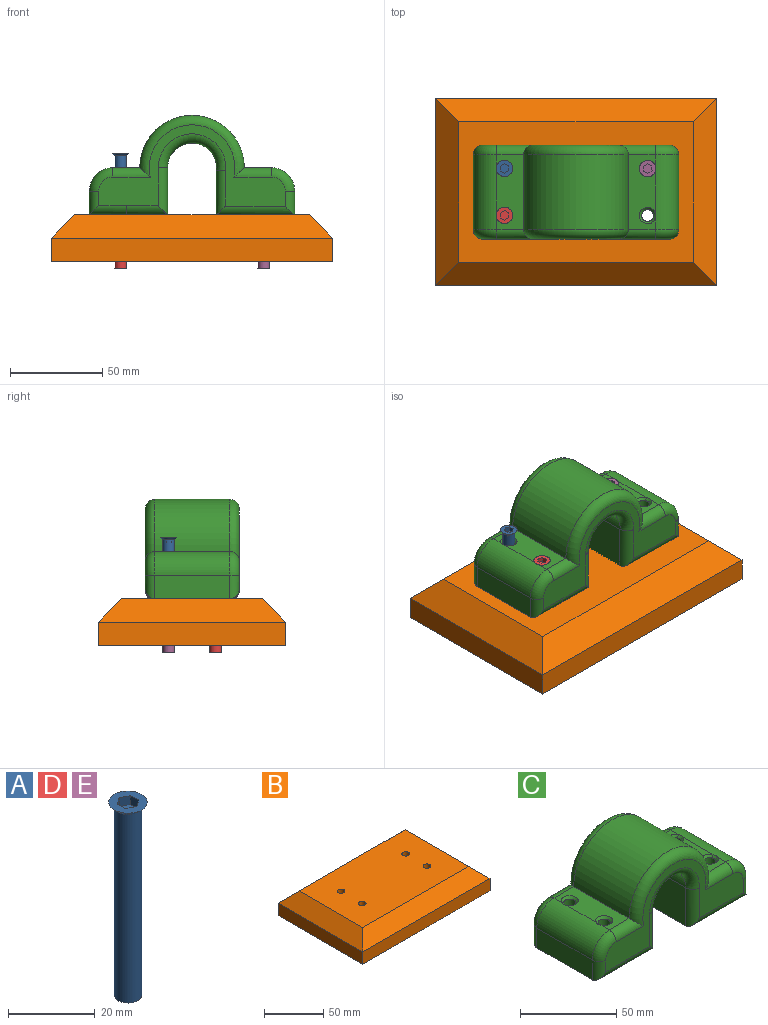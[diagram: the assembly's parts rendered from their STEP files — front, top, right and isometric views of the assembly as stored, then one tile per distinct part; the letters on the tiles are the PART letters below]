
ASSEMBLY  parts=5 mates=4
PART A: 11 faces, bbox 8.9x8.9x54.6 mm
  f0: plane 8.89x8.89mm, normal (0,0,1), area 43.8mm2, adj f3,f4,f5,f6,f7,f8,f9
  f1: cylinder r=3.17mm len=53.34mm, axis (0,0,-1), area 1064.1mm2, adj f2,f3
  f2: plane 6.35x6.35mm, normal (0,0,-1), area 31.7mm2, adj f1
  f3: cone r=4.45mm half-angle=45deg, axis (0,0,1), area 43mm2, adj f0,f1
  f4: plane 2.54x2.38mm, normal (-0.44,-0.9,0), area 6.7mm2, adj f0,f5,f9,f10
  f5: plane 2.54x2.2mm, normal (0.56,-0.83,0), area 6.7mm2, adj f0,f4,f6,f10
  f6: plane 2.64x2.54mm, normal (1,0.07,0), area 6.7mm2, adj f0,f5,f7,f10
  f7: plane 2.54x2.38mm, normal (0.44,0.9,0), area 6.7mm2, adj f0,f6,f8,f10
  f8: plane 2.54x2.2mm, normal (-0.56,0.83,0), area 6.7mm2, adj f0,f7,f9,f10
  f9: plane 2.64x2.54mm, normal (-1,-0.07,0), area 6.7mm2, adj f0,f4,f8,f10
  f10: plane 5.29x4.77mm, normal (0,0,1), area 18.2mm2, adj f4,f5,f6,f7,f8,f9
PART B: 14 faces, bbox 152.4x101.6x25.4 mm
  f0: plane 101.6x12.7mm, normal (-1,0,0), area 1290.3mm2, adj f1,f3,f5,f13
  f1: plane 152.4x12.7mm, normal (0,-1,0), area 1935.5mm2, adj f0,f2,f5,f11
  f2: plane 101.6x12.7mm, normal (1,0,0), area 1290.3mm2, adj f1,f3,f5,f12
  f3: plane 152.4x12.7mm, normal (0,1,0), area 1935.5mm2, adj f0,f2,f5,f10
  f4: plane 127x76.2mm, normal (0,0,1), area 9550.7mm2, adj f6,f7,f8,f9,f10,f11,f12,f13
  f5: plane 152.4x101.6mm, normal (0,0,-1), area 15357.2mm2, adj f0,f1,f2,f3,f6,f7,f8,f9
  f6: cylinder r=3.17mm len=25.4mm, axis (0,0,1), area 506.7mm2, adj f4,f5
  f7: cylinder r=3.17mm len=25.4mm, axis (0,0,1), area 506.7mm2, adj f4,f5
  f8: cylinder r=3.17mm len=25.4mm, axis (0,0,1), area 506.7mm2, adj f4,f5
  f9: cylinder r=3.17mm len=25.4mm, axis (0,0,1), area 506.7mm2, adj f4,f5
  f10: plane 152.4x12.7mm, normal (0,0.71,0.71), area 2509.1mm2, adj f3,f4,f12,f13
  f11: plane 152.4x12.7mm, normal (0,-0.71,0.71), area 2509.1mm2, adj f1,f4,f12,f13
  f12: plane 101.6x12.7mm, normal (0.71,0,0.71), area 1596.7mm2, adj f2,f4,f10,f11
  f13: plane 101.6x12.7mm, normal (-0.71,0,0.71), area 1596.7mm2, adj f0,f4,f10,f11
PART C: 53 faces, bbox 113.2x50.8x56.5 mm
  f0: plane 42.41x40.67mm, normal (0,0,-1), area 1659.1mm2, adj f4,f7,f15,f16,f20,f43
  f1: plane 40.64x19.98mm, normal (0.01,0,-1), area 748.8mm2, adj f2,f3,f13,f14,f30,f36
  f2: plane 40.64x22.33mm, normal (0,0,-1), area 907.4mm2, adj f1,f8,f28,f38
  f3: plane 40.64x12.7mm, normal (-1,0,-0.01), area 516.1mm2, adj f1,f9,f31,f34
  f4: plane 40.64x13.51mm, normal (1,0,0.01), area 549.2mm2, adj f0,f10,f19,f41
  f5: plane 40.64x14.57mm, normal (-0.01,0,1), area 469.3mm2, adj f10,f11,f23,f37,f49,f51
  f6: plane 40.64x14.57mm, normal (-0.01,0,1), area 469.3mm2, adj f9,f11,f27,f33,f45,f47
  f7: plane 40.64x24.47mm, normal (-1,0,-0.01), area 994.5mm2, adj f0,f12,f22,f44
  f8: plane 40.64x25.6mm, normal (1,0,0.01), area 1040.4mm2, adj f2,f12,f26,f40
  f9: cylinder r=12.7mm len=40.64mm, axis (0,-1,0), area 809mm2, adj f3,f6,f29,f32,f46,f48
  f10: cylinder r=12.7mm len=40.64mm, axis (0,1,0), area 809mm2, adj f4,f5,f21,f39,f50,f52
  f11: cylinder r=28.27mm len=56.54mm, axis (0,1,0), area 3609.4mm2, adj f5,f6,f25,f35
  f12: cylinder r=13.23mm len=40.64mm, axis (0,-1,0), area 1744.1mm2, adj f7,f8,f24,f42
  f13: cylinder r=3.17mm len=24.17mm, axis (-0.01,0,1), area 481.4mm2, adj f1,f47,f48
  f14: cylinder r=3.17mm len=24.17mm, axis (-0.01,0,1), area 481.4mm2, adj f1,f45,f46
  f15: cylinder r=3.17mm len=24.86mm, axis (-0.01,0,1), area 494.6mm2, adj f0,f49,f50
  f16: cylinder r=3.17mm len=24.86mm, axis (-0.01,0,1), area 494.6mm2, adj f0,f51,f52
  f17: plane 100.96x43.96mm, normal (0,-1,0), area 1344mm2, adj f19,f20,f21,f22,f23,f24,f25,f26
  f18: plane 100.96x43.96mm, normal (0,1,0), area 1344mm2, adj f32,f33,f34,f35,f36,f37,f38,f39
  f19: cylinder r=5.08mm len=13.55mm, axis (0.01,0,-1), area 87.4mm2, adj f4,f17,f20,f21
  f20: cylinder r=5.08mm len=42.4mm, axis (1,0,0), area 297.7mm2, adj f0,f17,f19,f22
  f21: torus R=7.62mm, axis (0,-1,0), area 136mm2, adj f10,f17,f19,f23
  f22: cylinder r=5.08mm len=24.5mm, axis (0.01,0,-1), area 174.2mm2, adj f7,f17,f20,f24
  f23: cylinder r=5.08mm len=20.24mm, axis (1,0,0.01), area 138.7mm2, adj f5,f17,f21,f25
  f24: torus R=18.31mm, axis (0,-1,0), area 389.3mm2, adj f12,f17,f22,f26
  f25: torus R=23.19mm, axis (0,-1,0), area 707.4mm2, adj f11,f17,f23,f27
  f26: cylinder r=5.08mm len=25.63mm, axis (-0.01,0,1), area 183.8mm2, adj f8,f17,f24,f28
  f27: cylinder r=5.08mm len=20.24mm, axis (1,0,0.01), area 138.7mm2, adj f6,f17,f25,f29
  f28: cylinder r=5.08mm len=22.37mm, axis (1,0,0), area 157.8mm2, adj f2,f17,f26,f30
  f29: torus R=7.62mm, axis (0,-1,0), area 136mm2, adj f9,f17,f27,f31
  f30: cylinder r=5.08mm len=20.04mm, axis (1,0,0.01), area 139.3mm2, adj f1,f17,f28,f31
  f31: cylinder r=5.08mm len=12.73mm, axis (-0.01,0,1), area 81.1mm2, adj f3,f17,f29,f30
  f32: torus R=7.62mm, axis (0,-1,0), area 136mm2, adj f9,f18,f33,f34
  f33: cylinder r=5.08mm len=20.24mm, axis (-1,0,-0.01), area 138.7mm2, adj f6,f18,f32,f35
  f34: cylinder r=5.08mm len=12.73mm, axis (0.01,0,-1), area 81.1mm2, adj f3,f18,f32,f36
  f35: torus R=23.19mm, axis (0,-1,0), area 707.4mm2, adj f11,f18,f33,f37
  f36: cylinder r=5.08mm len=20.04mm, axis (-1,0,-0.01), area 139.3mm2, adj f1,f18,f34,f38
  f37: cylinder r=5.08mm len=20.24mm, axis (-1,0,-0.01), area 138.7mm2, adj f5,f18,f35,f39
  f38: cylinder r=5.08mm len=22.37mm, axis (-1,0,0), area 157.8mm2, adj f2,f18,f36,f40
  f39: torus R=7.62mm, axis (0,-1,0), area 136mm2, adj f10,f18,f37,f41
  f40: cylinder r=5.08mm len=25.63mm, axis (0.01,0,-1), area 183.8mm2, adj f8,f18,f38,f42
  f41: cylinder r=5.08mm len=13.55mm, axis (-0.01,0,1), area 87.4mm2, adj f4,f18,f39,f43
  f42: torus R=18.31mm, axis (0,-1,0), area 389.3mm2, adj f12,f18,f40,f44
  f43: cylinder r=5.08mm len=42.4mm, axis (-1,0,0), area 297.7mm2, adj f0,f18,f41,f44
  f44: cylinder r=5.08mm len=24.5mm, axis (-0.01,0,1), area 174.2mm2, adj f7,f18,f42,f43
  f45: cone r=3.17mm half-angle=45deg, axis (-0.01,0,1), area 37.6mm2, adj f6,f14,f46
  f46: bspline ~3.4x1.68mm, area 5.4mm2, adj f9,f14,f45
  f47: cone r=3.17mm half-angle=45deg, axis (-0.01,0,1), area 37.6mm2, adj f6,f13,f48
  f48: bspline ~3.4x1.68mm, area 5.4mm2, adj f9,f13,f47
  f49: cone r=3.17mm half-angle=45deg, axis (-0.01,0,1), area 37.6mm2, adj f5,f15,f50
  f50: bspline ~3.4x1.67mm, area 5.4mm2, adj f10,f15,f49
  f51: cone r=3.17mm half-angle=45deg, axis (-0.01,0,1), area 37.6mm2, adj f5,f16,f52
  f52: bspline ~3.4x1.67mm, area 5.4mm2, adj f10,f16,f51
PART D: same geometry as A
PART E: same geometry as A
PLACE A t=(-24.35,-27.28,-74.08)mm
PLACE B t=(14.36,-39.98,-77.89)mm
PLACE C rot(axis=(0,1,0),0.4deg) t=(14.37,-2.02,-53.16)mm
PLACE D t=(-24.35,-52.68,-81.7)mm
PLACE E t=(53.1,-27.42,-81.7)mm
MATE pin_slot D.f1 <-> C.f14  axis (0,0,-1) through (-24.35,-52.68,-81.7)mm
MATE pin_slot A.f1 <-> C.f13  axis (0,0,-1) through (-24.35,-27.28,-74.08)mm
MATE pin_slot E.f1 <-> C.f16  axis (0,0,-1) through (53.1,-27.42,-81.7)mm
MATE cylindrical C.f14 <-> B.f6  axis (0,0,-1) through (-24.35,-52.68,-52.49)mm
